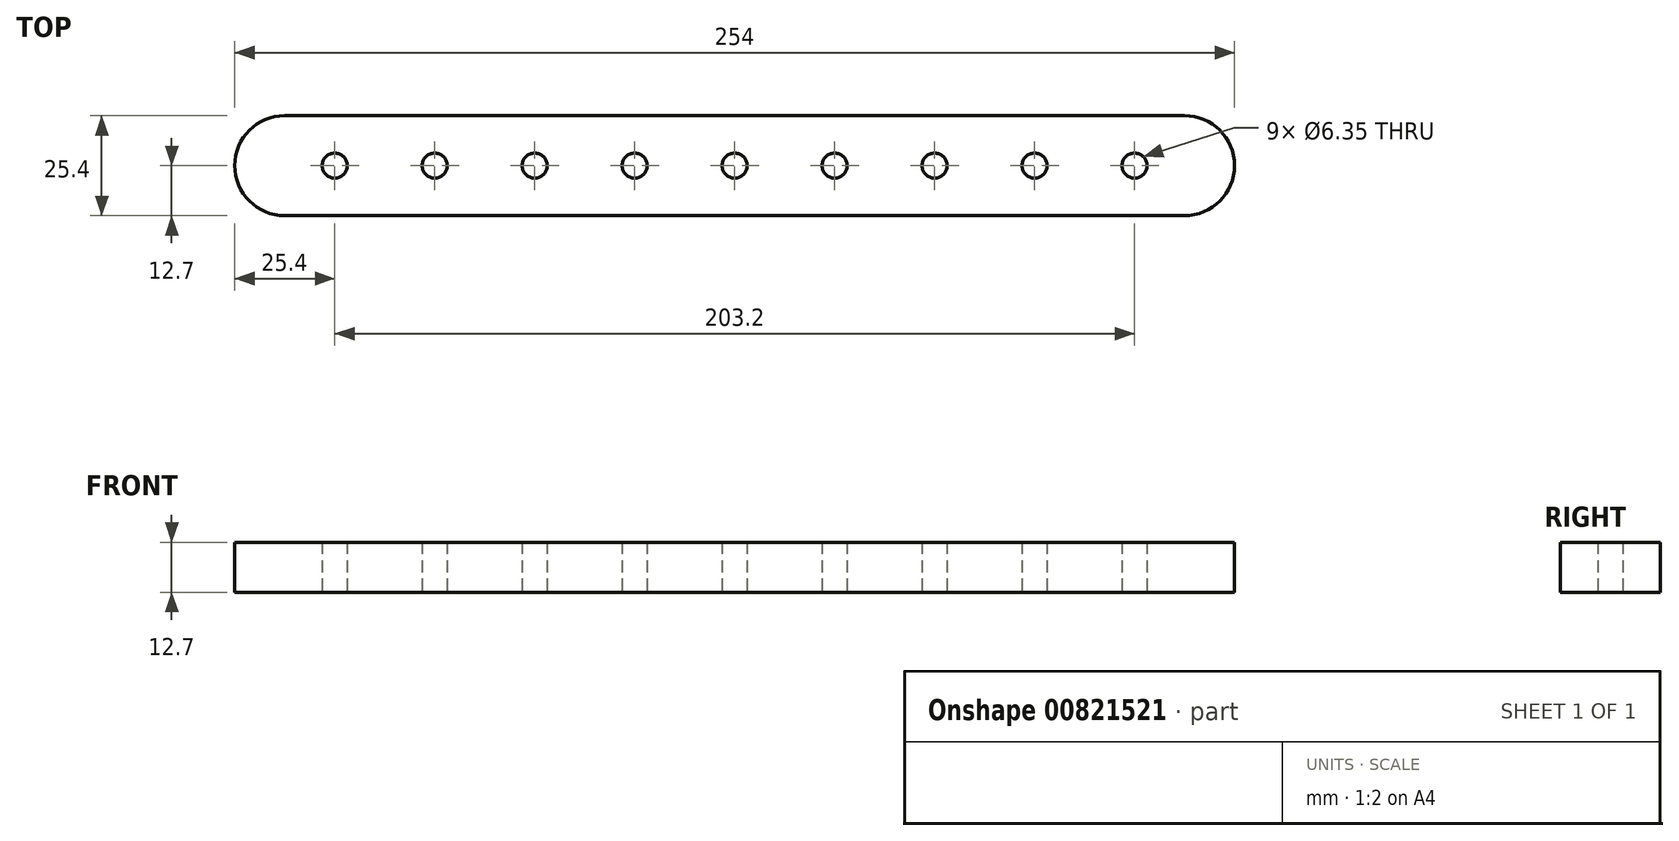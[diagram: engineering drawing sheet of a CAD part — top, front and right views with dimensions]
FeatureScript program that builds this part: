
annotation { "Feature Type Name" : "Feature", "Feature Type Description" : "" }
export const myFeature = defineFeature(function(context is Context, id is Id, definition is map)
    precondition{}
    {
        {
            var Q0;
            Q0=qCreatedBy(makeId("Top.planeOp"),FACE);
            var sketch = newSketch(context, id + "F0", { "sketchPlane" : qUnion([Q0])});
            skLineSegment(sketch, "E0.bottom", {"start": v(114.3, -12.7) * mm, "end": v(-114.3, -12.7) * mm});
            skLineSegment(sketch, "E0.top", {"start": v(114.3, 12.7) * mm, "end": v(-114.3, 12.7) * mm});
            skLineSegment(sketch, "E0.left", {"start": v(127, 0) * mm, "end": v(127, 0) * mm});
            skLineSegment(sketch, "E0.right", {"start": v(-127, 0) * mm, "end": v(-127, 0) * mm});
            skPoint(sketch, "E0.middle", {"position": v(0, 0) * mm});
            skPoint(sketch, "E1.visualSharp", {"position": v(-127, 12.7) * mm});
            skArc(sketch, "E1.filletArc", {"start": v(-114.3, 12.7) * mm, "mid": v(-123.28, 8.98) * mm, "end": v(-127, 0) * mm});
            skPoint(sketch, "E2.visualSharp", {"position": v(-127, -12.7) * mm});
            skArc(sketch, "E2.filletArc", {"start": v(-127, 0) * mm, "mid": v(-123.28, -8.98) * mm, "end": v(-114.3, -12.7) * mm});
            skPoint(sketch, "E3.visualSharp", {"position": v(127, 12.7) * mm});
            skArc(sketch, "E3.filletArc", {"start": v(127, 0) * mm, "mid": v(123.28, 8.98) * mm, "end": v(114.3, 12.7) * mm});
            skPoint(sketch, "E4.visualSharp", {"position": v(127, -12.7) * mm});
            skArc(sketch, "E4.filletArc", {"start": v(114.3, -12.7) * mm, "mid": v(123.28, -8.98) * mm, "end": v(127, 0) * mm});
            skCircle(sketch, "E5", {"center": v(0, 0) * mm, "radius": 3.18 * mm});
            skCircle(sketch, "E6.1.0.0", {"center": v(25.4, 0) * mm, "radius": 3.18 * mm});
            skCircle(sketch, "E6.2.0.0", {"center": v(50.8, 0) * mm, "radius": 3.18 * mm});
            skCircle(sketch, "E6.3.0.0", {"center": v(76.2, 0) * mm, "radius": 3.18 * mm});
            skCircle(sketch, "E6.4.0.0", {"center": v(101.6, 0) * mm, "radius": 3.18 * mm});
            skLineSegment(sketch, "E6.direction1", {"start": v(0, 0) * mm, "end": v(25.4, 0) * mm, "construction": true});
            skCircle(sketch, "E7.1.0.0", {"center": v(-25.4, 0) * mm, "radius": 3.18 * mm});
            skCircle(sketch, "E7.2.0.0", {"center": v(-50.8, 0) * mm, "radius": 3.18 * mm});
            skCircle(sketch, "E7.3.0.0", {"center": v(-76.2, 0) * mm, "radius": 3.18 * mm});
            skCircle(sketch, "E7.4.0.0", {"center": v(-101.6, 0) * mm, "radius": 3.18 * mm});
            skLineSegment(sketch, "E7.direction1", {"start": v(0, 0) * mm, "end": v(-25.4, 0) * mm, "construction": true});
            skSolve(sketch);
        }
        {
            var Q0;
            Q0=makeQuery(id+"F0.imprint","IMPRINT",FACE,{"disambiguationData":[TD([[makeQuery(id+"F0.imprint","IMPRINT",EDGE,{"derivedFrom":sQuery(id+"F0.wireOp",EDGE,"E0.bottom")}),-1.0]])]});
            extrude(context, id + "F1", {"entities" : qUnion([Q0]), "depth" : 12.7 * mm, "offsetDistance" : 25.4 * mm});
        }
    });
